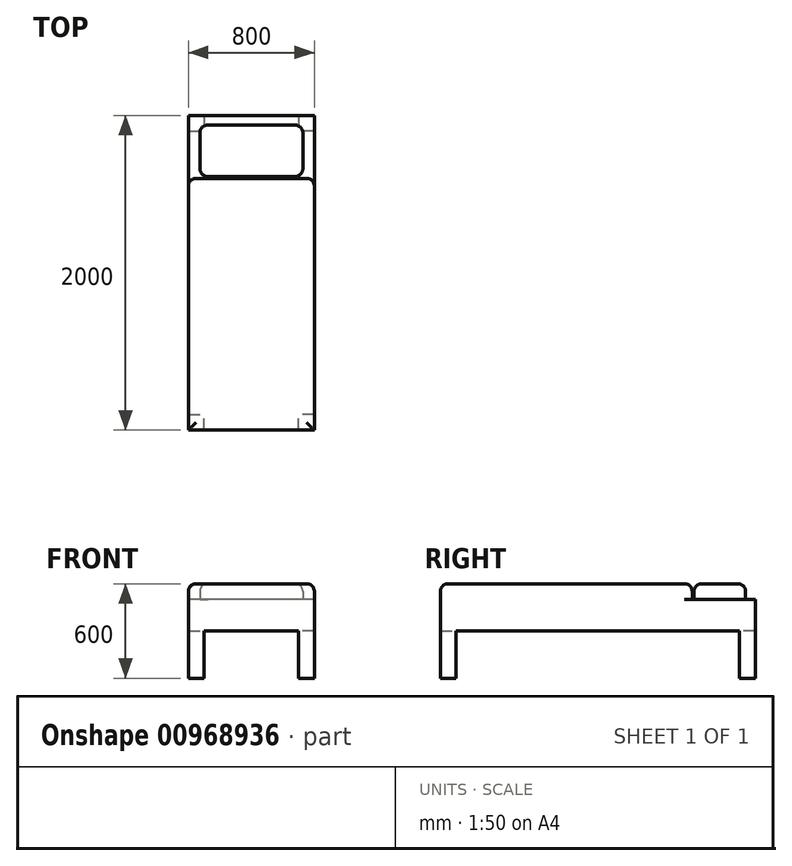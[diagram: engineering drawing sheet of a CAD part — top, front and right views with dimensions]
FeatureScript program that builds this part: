
annotation { "Feature Type Name" : "Feature", "Feature Type Description" : "" }
export const myFeature = defineFeature(function(context is Context, id is Id, definition is map)
    precondition{}
    {
        {
            var Q0;
            Q0=qCreatedBy(makeId("Top.planeOp"),FACE);
            var sketch = newSketch(context, id + "F0", { "sketchPlane" : qUnion([Q0])});
            skLineSegment(sketch, "E0.bottom", {"start": v(400, 1000) * mm, "end": v(-400, 1000) * mm});
            skLineSegment(sketch, "E0.top", {"start": v(400, -1000) * mm, "end": v(-400, -1000) * mm});
            skLineSegment(sketch, "E0.left", {"start": v(400, 1000) * mm, "end": v(400, -1000) * mm});
            skLineSegment(sketch, "E0.right", {"start": v(-400, 1000) * mm, "end": v(-400, -1000) * mm});
            skPoint(sketch, "E0.middle", {"position": v(0, 0) * mm});
            skSolve(sketch);
        }
        {
            var Q0;
            Q0=makeQuery(id+"F0.imprint","IMPRINT",FACE,{"disambiguationData":[TD([[makeQuery(id+"F0.imprint","IMPRINT",EDGE,{"derivedFrom":sQuery(id+"F0.wireOp",EDGE,"E0.bottom")}),1.0]])]});
            extrude(context, id + "F1", {"entities" : qUnion([Q0]), "depth" : 200 * mm, "offsetDistance" : 25 * mm});
        }
        {
            var Q0;
            Q0=makeQuery(id+"F1.opExtrude","CAP_FACE",FACE,{"disambiguationData":[OSD([sQuery(id+"F0.wireOp",EDGE,"E0.bottom"),sQuery(id+"F0.wireOp",EDGE,"E0.top"),sQuery(id+"F0.wireOp",EDGE,"E0.left"),sQuery(id+"F0.wireOp",EDGE,"E0.right")])],"isStart":true});
            var sketch = newSketch(context, id + "F2", { "sketchPlane" : qUnion([Q0])});
            skLineSegment(sketch, "E1.bottom", {"start": v(400, 1000) * mm, "end": v(300, 1000) * mm});
            skLineSegment(sketch, "E1.top", {"start": v(400, 900) * mm, "end": v(300, 900) * mm});
            skLineSegment(sketch, "E1.left", {"start": v(400, 1000) * mm, "end": v(400, 900) * mm});
            skLineSegment(sketch, "E1.right", {"start": v(300, 1000) * mm, "end": v(300, 900) * mm});
            skLineSegment(sketch, "E2.bottom", {"start": v(-400, 1000) * mm, "end": v(-300, 1000) * mm});
            skLineSegment(sketch, "E2.top", {"start": v(-400, 900) * mm, "end": v(-300, 900) * mm});
            skLineSegment(sketch, "E2.left", {"start": v(-400, 1000) * mm, "end": v(-400, 900) * mm});
            skLineSegment(sketch, "E2.right", {"start": v(-300, 1000) * mm, "end": v(-300, 900) * mm});
            skLineSegment(sketch, "E3.bottom", {"start": v(-400, -1000) * mm, "end": v(-300, -1000) * mm});
            skLineSegment(sketch, "E3.top", {"start": v(-400, -900) * mm, "end": v(-300, -900) * mm});
            skLineSegment(sketch, "E3.left", {"start": v(-400, -1000) * mm, "end": v(-400, -900) * mm});
            skLineSegment(sketch, "E3.right", {"start": v(-300, -1000) * mm, "end": v(-300, -900) * mm});
            skLineSegment(sketch, "E4.bottom", {"start": v(400, -1000) * mm, "end": v(300, -1000) * mm});
            skLineSegment(sketch, "E4.top", {"start": v(400, -900) * mm, "end": v(300, -900) * mm});
            skLineSegment(sketch, "E4.left", {"start": v(400, -1000) * mm, "end": v(400, -900) * mm});
            skLineSegment(sketch, "E4.right", {"start": v(300, -1000) * mm, "end": v(300, -900) * mm});
            skSolve(sketch);
        }
        {
            var Q0;
            Q0 = qSketchRegion(id + "F2", true);
            extrude(context, id + "F3", {"entities" : qUnion([Q0]), "operationType" : NewBodyOperationType.ADD, "depth" : 300 * mm, "offsetDistance" : 25 * mm});
        }
        {
            var Q0;
            Q0=makeQuery(id+"F1.opExtrude","CAP_FACE",FACE,{"disambiguationData":[OSD([sQuery(id+"F0.wireOp",EDGE,"E0.bottom"),sQuery(id+"F0.wireOp",EDGE,"E0.top"),sQuery(id+"F0.wireOp",EDGE,"E0.left"),sQuery(id+"F0.wireOp",EDGE,"E0.right")])],"isStart":false});
            var sketch = newSketch(context, id + "F4", { "sketchPlane" : qUnion([Q0])});
            skLineSegment(sketch, "E5.bottom", {"start": v(400, -1000) * mm, "end": v(-400, -1000) * mm});
            skLineSegment(sketch, "E5.top", {"start": v(400, 600) * mm, "end": v(-400, 600) * mm});
            skLineSegment(sketch, "E5.left", {"start": v(400, -1000) * mm, "end": v(400, 600) * mm});
            skLineSegment(sketch, "E5.right", {"start": v(-400, -1000) * mm, "end": v(-400, 600) * mm});
            skSolve(sketch);
        }
        {
            var Q0;
            Q0=makeQuery(id+"F4.imprint","IMPRINT",FACE,{"disambiguationData":[TD([[makeQuery(id+"F4.imprint","IMPRINT",EDGE,{"derivedFrom":sQuery(id+"F4.wireOp",EDGE,"E5.bottom")}),-1.0]])]});
            extrude(context, id + "F5", {"entities" : qUnion([Q0]), "operationType" : NewBodyOperationType.ADD, "depth" : 100 * mm, "offsetDistance" : 25 * mm});
        }
        {
            var Q0;
            Q0=makeQuery(id+"F5.opExtrude","CAP_EDGE",EDGE,{"disambiguationData":[OSD([sQuery(id+"F4.wireOp",EDGE,"E5.left")])],"isStart":false});
            var Q1;
            Q1=makeQuery(id+"F5.opExtrude","CAP_EDGE",EDGE,{"disambiguationData":[OSD([sQuery(id+"F4.wireOp",EDGE,"E5.bottom")])],"isStart":false});
            var Q2;
            Q2=makeQuery(id+"F5.opExtrude","CAP_EDGE",EDGE,{"disambiguationData":[OSD([sQuery(id+"F4.wireOp",EDGE,"E5.right")])],"isStart":false});
            var Q3;
            Q3=makeQuery(id+"F5.opExtrude","CAP_EDGE",EDGE,{"disambiguationData":[OSD([sQuery(id+"F4.wireOp",EDGE,"E5.top")])],"isStart":false});
            var Q4;
            Q4=makeQuery(id+"F5.opExtrude","SWEPT_EDGE",EDGE,{"disambiguationData":[OSD([sQuery(id+"F0.wireOp",EDGE,"E0.left"),sQuery(id+"F4.wireOp",EDGE,"E5.top"),sQuery(id+"F4.wireOp",EDGE,"E5.left")])]});
            var Q5;
            Q5=makeQuery(id+"F5.opExtrude","SWEPT_EDGE",EDGE,{"disambiguationData":[OSD([sQuery(id+"F0.wireOp",EDGE,"E0.right"),sQuery(id+"F4.wireOp",EDGE,"E5.top"),sQuery(id+"F4.wireOp",EDGE,"E5.right")])]});
            fillet(context, id + "F6", {"entities" : qUnion([Q0, Q1, Q2, Q3, Q4, Q5]), "radius" : 50 * mm, "tangentPropagation" : true, "allowEdgeOverflow" : false});
        }
        {
            var Q0;
            Q0=makeQuery(id+"F1.opExtrude","CAP_FACE",FACE,{"disambiguationData":[OSD([sQuery(id+"F0.wireOp",EDGE,"E0.bottom"),sQuery(id+"F0.wireOp",EDGE,"E0.top"),sQuery(id+"F0.wireOp",EDGE,"E0.left"),sQuery(id+"F0.wireOp",EDGE,"E0.right")])],"isStart":false});
            var sketch = newSketch(context, id + "F7", { "sketchPlane" : qUnion([Q0])});
            skLineSegment(sketch, "E6.bottom", {"start": v(326.8, 938.72) * mm, "end": v(-326.8, 938.72) * mm});
            skLineSegment(sketch, "E6.top", {"start": v(326.8, 611.28) * mm, "end": v(-326.8, 611.28) * mm});
            skLineSegment(sketch, "E6.left", {"start": v(326.8, 938.72) * mm, "end": v(326.8, 611.28) * mm});
            skLineSegment(sketch, "E6.right", {"start": v(-326.8, 938.72) * mm, "end": v(-326.8, 611.28) * mm});
            skPoint(sketch, "E6.middle", {"position": v(0, 775) * mm});
            skPoint(sketch, "E6.middle.positionSnap0", {"position": v(-400, 775) * mm});
            skPoint(sketch, "E6.centerSnap0", {"position": v(-400, 775) * mm});
            skSolve(sketch);
        }
        {
            var Q0;
            Q0 = qSketchRegion(id + "F7", true);
            extrude(context, id + "F8", {"entities" : qUnion([Q0]), "operationType" : NewBodyOperationType.ADD, "depth" : 100 * mm, "offsetDistance" : 25 * mm});
        }
        {
            var Q0;
            Q0=makeQuery(id+"F8.opExtrude","CAP_EDGE",EDGE,{"disambiguationData":[OSD([sQuery(id+"F7.wireOp",EDGE,"E6.left")])],"isStart":false});
            var Q1;
            Q1=makeQuery(id+"F8.opExtrude","SWEPT_EDGE",EDGE,{"disambiguationData":[OSD([sQuery(id+"F7.wireOp",EDGE,"E6.bottom"),sQuery(id+"F7.wireOp",EDGE,"E6.left")])]});
            var Q2;
            Q2=makeQuery(id+"F8.opExtrude","CAP_EDGE",EDGE,{"disambiguationData":[OSD([sQuery(id+"F7.wireOp",EDGE,"E6.bottom")])],"isStart":false});
            var Q3;
            Q3=makeQuery(id+"F8.opExtrude","SWEPT_EDGE",EDGE,{"disambiguationData":[OSD([sQuery(id+"F7.wireOp",EDGE,"E6.bottom"),sQuery(id+"F7.wireOp",EDGE,"E6.right")])]});
            var Q4;
            Q4=makeQuery(id+"F8.opExtrude","CAP_EDGE",EDGE,{"disambiguationData":[OSD([sQuery(id+"F7.wireOp",EDGE,"E6.right")])],"isStart":false});
            var Q5;
            Q5=makeQuery(id+"F8.opExtrude","SWEPT_EDGE",EDGE,{"disambiguationData":[OSD([sQuery(id+"F7.wireOp",EDGE,"E6.top"),sQuery(id+"F7.wireOp",EDGE,"E6.right")])]});
            var Q6;
            Q6=makeQuery(id+"F8.opExtrude","CAP_EDGE",EDGE,{"disambiguationData":[OSD([sQuery(id+"F7.wireOp",EDGE,"E6.top")])],"isStart":false});
            var Q7;
            Q7=makeQuery(id+"F8.opExtrude","SWEPT_EDGE",EDGE,{"disambiguationData":[OSD([sQuery(id+"F7.wireOp",EDGE,"E6.top"),sQuery(id+"F7.wireOp",EDGE,"E6.left")])]});
            fillet(context, id + "F9", {"entities" : qUnion([Q0, Q1, Q2, Q3, Q4, Q5, Q6, Q7]), "radius" : 50 * mm, "tangentPropagation" : true, "allowEdgeOverflow" : false});
        }
    });
